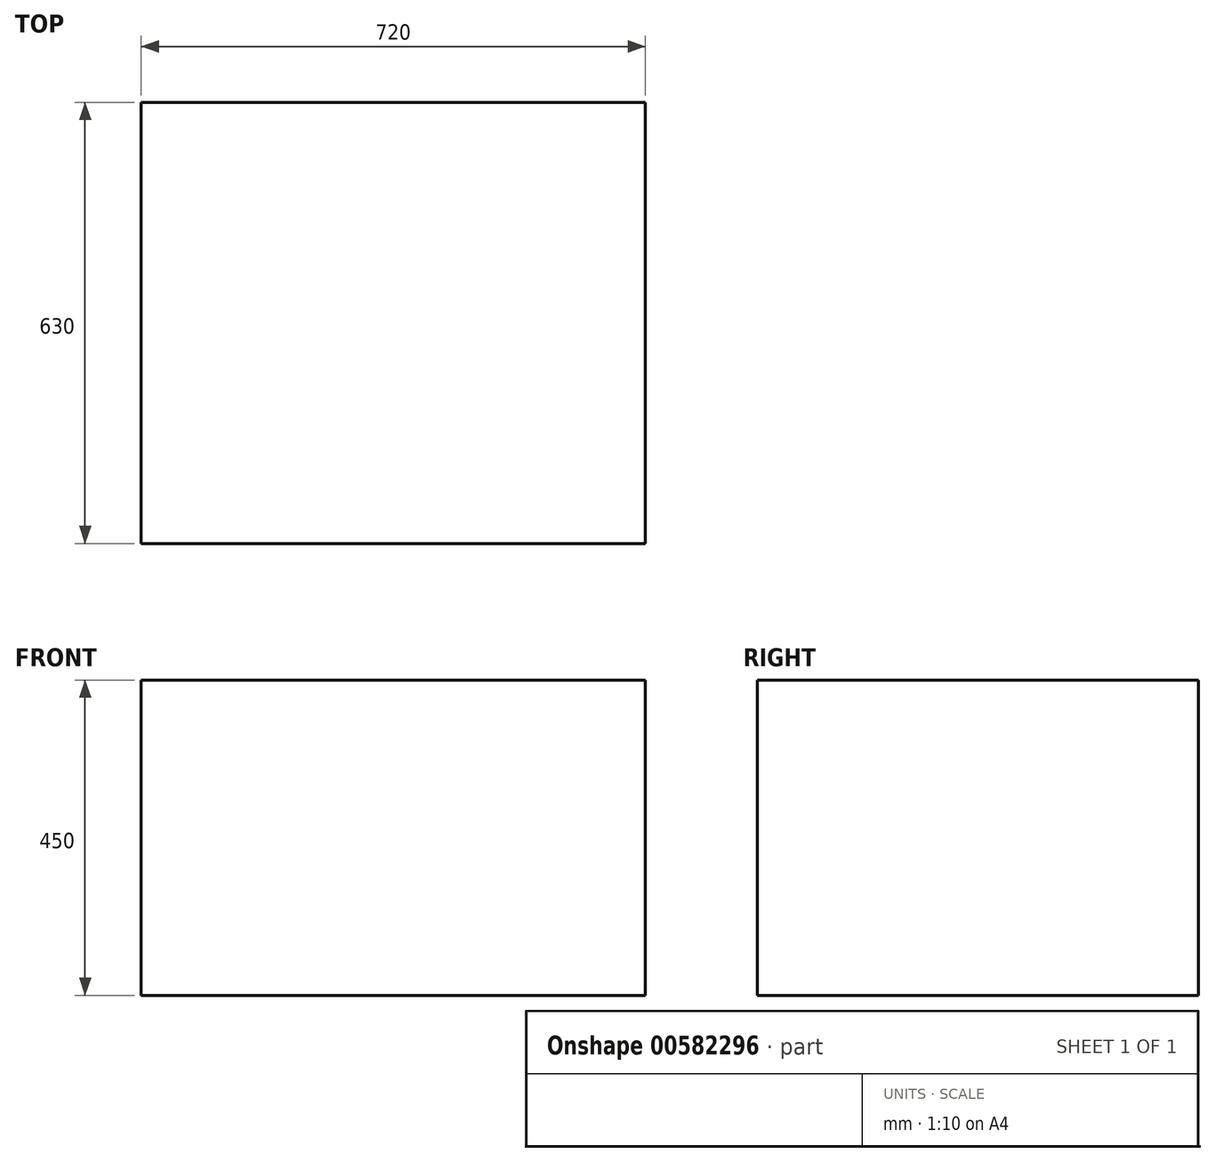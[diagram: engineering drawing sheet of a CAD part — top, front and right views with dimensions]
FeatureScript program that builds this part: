
annotation { "Feature Type Name" : "Feature", "Feature Type Description" : "" }
export const myFeature = defineFeature(function(context is Context, id is Id, definition is map)
    precondition{}
    {
        {
            var Q0;
            Q0=qCreatedBy(makeId("Top.planeOp"),FACE);
            cPlane(context, id + "F0", {"entities" : qUnion([Q0]), "cplaneType" : CPlaneType.OFFSET, "offset" : 330 * mm, "oppositeDirection" : true, "width" : 150 * mm, "height" : 150 * mm});
        }
        {
            var Q0;
            Q0=qCreatedBy(makeId("Front.planeOp"),FACE);
            var sketch = newSketch(context, id + "F1", { "sketchPlane" : qUnion([Q0])});
            skLineSegment(sketch, "E0", {"start": v(0, 0) * mm, "end": v(-670, 0) * mm});
            skLineSegment(sketch, "E1", {"start": v(-670, 0) * mm, "end": v(-735.9, 47.4) * mm});
            skLineSegment(sketch, "E2", {"start": v(-670, 0) * mm, "end": v(-720, 0) * mm});
            skLineSegment(sketch, "E3", {"start": v(-720, 0) * mm, "end": v(-824, 310) * mm});
            skLineSegment(sketch, "E4", {"start": v(-702.95, 23.7) * mm, "end": v(-720, 0) * mm, "construction": true});
            skLineSegment(sketch, "E5", {"start": v(-824, 310) * mm, "end": v(-810, 330) * mm});
            skLineSegment(sketch, "E6", {"start": v(-810, 330) * mm, "end": v(-810, 680) * mm});
            skLineSegment(sketch, "E7", {"start": v(-810, 680) * mm, "end": v(-280, 950) * mm});
            skLineSegment(sketch, "E8", {"start": v(-810, 330) * mm, "end": v(-850.96, 358.67) * mm});
            skLineSegment(sketch, "E9", {"start": v(-850.96, 358.67) * mm, "end": v(-891.1, 301.33) * mm});
            skLineSegment(sketch, "E10", {"start": v(0, 0) * mm, "end": v(0, 450) * mm});
            skLineSegment(sketch, "E11", {"start": v(0, 450) * mm, "end": v(-280, 450) * mm});
            skLineSegment(sketch, "E12", {"start": v(-280, 450) * mm, "end": v(-280, 950) * mm});
            skSolve(sketch);
        }
        {
            var Q0;
            Q0=qCreatedBy(makeId("Top.planeOp"),FACE);
            var sketch = newSketch(context, id + "F2", { "sketchPlane" : qUnion([Q0])});
            skLineSegment(sketch, "E13", {"start": v(0, 199) * mm, "end": v(-720, 199) * mm, "construction": true});
            skLineSegment(sketch, "E14", {"start": v(0, 230) * mm, "end": v(-720, 230) * mm, "construction": true});
            skLineSegment(sketch, "E15", {"start": v(0, 315) * mm, "end": v(-720, 315) * mm});
            skPoint(sketch, "E16", {"position": v(-30, 189) * mm});
            skPoint(sketch, "E17", {"position": v(-490, 189) * mm});
            skPoint(sketch, "E18.MirrorP", {"position": v(-30, -189) * mm});
            skLineSegment(sketch, "E19.MirrorCS", {"start": v(0, -230) * mm, "end": v(-720, -230) * mm, "construction": true});
            skLineSegment(sketch, "E20.MirrorCS", {"start": v(0, -199) * mm, "end": v(-720, -199) * mm, "construction": true});
            skPoint(sketch, "E21.MirrorP", {"position": v(-490, -189) * mm});
            skLineSegment(sketch, "E22.MirrorCS", {"start": v(0, -315) * mm, "end": v(-720, -315) * mm});
            skSolve(sketch);
        }
        {
            var Q0;
            Q0=qCreatedBy(makeId("Top.planeOp"),FACE);
            var sketch = newSketch(context, id + "F3", { "sketchPlane" : qUnion([Q0])});
            skLineSegment(sketch, "E23.bottom", {"start": v(-720, 315) * mm, "end": v(0, 315) * mm});
            skLineSegment(sketch, "E23.top", {"start": v(-720, -315) * mm, "end": v(0, -315) * mm});
            skLineSegment(sketch, "E23.left", {"start": v(-720, 315) * mm, "end": v(-720, -315) * mm});
            skLineSegment(sketch, "E23.right", {"start": v(0, 315) * mm, "end": v(0, -315) * mm});
            skSolve(sketch);
        }
        {
            var Q0;
            Q0=makeQuery(id+"F3.imprint","IMPRINT",FACE,{"disambiguationData":[TD([[makeQuery(id+"F3.imprint","IMPRINT",EDGE,{"derivedFrom":sQuery(id+"F3.wireOp",EDGE,"E23.bottom")}),-1.0]])]});
            var Q1;
            Q1=sQuery(id+"F1.wireOp",VERTEX,"E12.start");
            extrude(context, id + "F4", {"entities" : qUnion([Q0]), "endBound" : BoundingType.UP_TO_VERTEX, "depth" : 25 * mm, "endBoundEntityVertex" : qUnion([Q1]), "offsetDistance" : 25 * mm});
        }
    });
